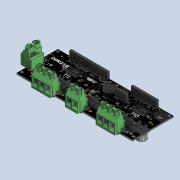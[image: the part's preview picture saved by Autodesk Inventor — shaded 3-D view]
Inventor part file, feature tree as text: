
AUTODESK INVENTOR PART (.ipt)
format: ipt  version: 2020 (Build 240168000, 168)  size: 21,689,856 bytes
history: native  units: mm
features: other x279, sketch x3
ambient origin geometry x8: Origin, YZ Plane, XZ Plane, XY Plane, X Axis, Y Axis, Z Axis, Center Point
bodies: Solid1 (feature_tree)
feature tree (282):
  other  "PCBasembly.iam"
  other  "Board.ipt:1"
  other  "R58.iam:1::RES_0603_(1608_metric).ipt:1"
  other  "LED1.iam:1::LED_0603_APT1608_GREEN.ipt:1"
  other  "TP3.iam:1::886587760.iam:1::Cylinder.ipt:1"
  other  "TP2.iam:1::886587760.iam:1::Cylinder.ipt:1"
  other  "TP1.iam:1::886587632.iam:1::Cylinder_1.ipt:1"
  other  "C48.iam:1::899959440.iam:1::Extruded.ipt:1"
  other  "C48.iam:1::899959304.iam:1::Extruded_1.ipt:1"
  other  "C48.iam:1::899959304.iam:2::Extruded_1.ipt:1"
  other  "R34.iam:1::RES_0603_(1608_metric).ipt:1"
  other  "R33.iam:1::RES_0603_(1608_metric).ipt:1"
  other  "R32.iam:1::RES_0603_(1608_metric).ipt:1"
  other  "R48.iam:1::RES_0603_(1608_metric).ipt:1"
  other  "R46.iam:1::899960256.iam:1::Extruded_3.ipt:1"
  other  "R46.iam:1::899960392.iam:1::Extruded_4.ipt:1"
  other  "R46.iam:1::899960256.iam:2::Extruded_3.ipt:1"
  other  "R45.iam:1::899960256.iam:1::Extruded_3.ipt:1"
  other  "R45.iam:1::899960392.iam:1::Extruded_4.ipt:1"
  other  "R45.iam:1::899960256.iam:2::Extruded_3.ipt:1"
  other  "R43.iam:1::RES_0603_(1608_metric).ipt:1"
  other  "R42.iam:1::RES_0603_(1608_metric).ipt:1"
  other  "R41.iam:1::RES_0603_(1608_metric).ipt:1"
  other  "R40.iam:1::RES_0603_(1608_metric).ipt:1"
  other  "R39.iam:1::RES_0603_(1608_metric).ipt:1"
  other  "R38.iam:1::RES_0603_(1608_metric).ipt:1"
  other  "R37.iam:1::RES_0603_(1608_metric).ipt:1"
  other  "R36.iam:1::RES_0603_(1608_metric).ipt:1"
  other  "R35.iam:1::RES_0603_(1608_metric).ipt:1"
  other  "C57.iam:1::899958488.iam:1::Extruded_5.ipt:1"
  other  "C57.iam:1::899958352.iam:1::Extruded_6.ipt:1"
  other  "C57.iam:1::899958352.iam:2::Extruded_6.ipt:1"
  other  "C56.iam:1::899958488.iam:1::Extruded_5.ipt:1"
  other  "C56.iam:1::899958352.iam:1::Extruded_6.ipt:1"
  other  "C56.iam:1::899958352.iam:2::Extruded_6.ipt:1"
  other  "C44.iam:1::899959032.iam:1::Extruded_7.ipt:1"
  other  "C44.iam:1::899959168.iam:1::Extruded_8.ipt:1"
  other  "C44.iam:1::899959032.iam:2::Extruded_7.ipt:1"
  other  "C52.iam:1::899959440.iam:1::Extruded.ipt:1"
  other  "C52.iam:1::899959304.iam:1::Extruded_1.ipt:1"
  other  "C52.iam:1::899959304.iam:2::Extruded_1.ipt:1"
  other  "C51.iam:1::899959440.iam:1::Extruded.ipt:1"
  other  "C51.iam:1::899959304.iam:1::Extruded_1.ipt:1"
  other  "C51.iam:1::899959304.iam:2::Extruded_1.ipt:1"
  other  "C50.iam:1::899959440.iam:1::Extruded.ipt:1"
  other  "C50.iam:1::899959304.iam:1::Extruded_1.ipt:1"
  other  "C50.iam:1::899959304.iam:2::Extruded_1.ipt:1"
  other  "C49.iam:1::899959440.iam:1::Extruded.ipt:1"
  other  "C49.iam:1::899959304.iam:1::Extruded_1.ipt:1"
  other  "C49.iam:1::899959304.iam:2::Extruded_1.ipt:1"
  other  "C47.iam:1::899959440.iam:1::Extruded.ipt:1"
  other  "C47.iam:1::899959304.iam:1::Extruded_1.ipt:1"
  other  "C47.iam:1::899959304.iam:2::Extruded_1.ipt:1"
  other  "C46.iam:1::899959440.iam:1::Extruded.ipt:1"
  other  "C46.iam:1::899959304.iam:1::Extruded_1.ipt:1"
  other  "C46.iam:1::899959304.iam:2::Extruded_1.ipt:1"
  other  "C45.iam:1::899959440.iam:1::Extruded.ipt:1"
  other  "C45.iam:1::899959304.iam:1::Extruded_1.ipt:1"
  other  "C45.iam:1::899959304.iam:2::Extruded_1.ipt:1"
  other  "C55.iam:1::899959032.iam:1::Extruded_7.ipt:1"
  other  "C55.iam:1::899959168.iam:1::Extruded_8.ipt:1"
  other  "C55.iam:1::899959032.iam:2::Extruded_7.ipt:1"
  other  "C18.iam:1::CAP_Alum_Elec_Size_G.ipt:1"
  other  "C17.iam:1::CAP_Alum_Elec_Size_G.ipt:1"
  other  "C16.iam:1::CAP_Alum_Elec_Size_G.ipt:1"
  other  "C43.iam:1::899958488.iam:1::Extruded_5.ipt:1"
  other  "C43.iam:1::899958352.iam:1::Extruded_6.ipt:1"
  other  "C43.iam:1::899958352.iam:2::Extruded_6.ipt:1"
  other  "C1.iam:1::899958488.iam:1::Extruded_5.ipt:1"
  other  "C1.iam:1::899958352.iam:1::Extruded_6.ipt:1"
  other  "C1.iam:1::899958352.iam:2::Extruded_6.ipt:1"
  other  "C2.iam:1::899958488.iam:1::Extruded_5.ipt:1"
  other  "C2.iam:1::899958352.iam:1::Extruded_6.ipt:1"
  other  "C2.iam:1::899958352.iam:2::Extruded_6.ipt:1"
  other  "C3.iam:1::899958488.iam:1::Extruded_5.ipt:1"
  other  "C3.iam:1::899958352.iam:1::Extruded_6.ipt:1"
  other  "C3.iam:1::899958352.iam:2::Extruded_6.ipt:1"
  other  "C4.iam:1::899958488.iam:1::Extruded_5.ipt:1"
  other  "C4.iam:1::899958352.iam:1::Extruded_6.ipt:1"
  other  "C4.iam:1::899958352.iam:2::Extruded_6.ipt:1"
  other  "C5.iam:1::899958488.iam:1::Extruded_5.ipt:1"
  other  "C5.iam:1::899958352.iam:1::Extruded_6.ipt:1"
  other  "C5.iam:1::899958352.iam:2::Extruded_6.ipt:1"
  other  "C6.iam:1::899958488.iam:1::Extruded_5.ipt:1"
  other  "C6.iam:1::899958352.iam:1::Extruded_6.ipt:1"
  other  "C6.iam:1::899958352.iam:2::Extruded_6.ipt:1"
  other  "C7.iam:1::899958488.iam:1::Extruded_5.ipt:1"
  other  "C7.iam:1::899958352.iam:1::Extruded_6.ipt:1"
  other  "C7.iam:1::899958352.iam:2::Extruded_6.ipt:1"
  other  "C8.iam:1::899958488.iam:1::Extruded_5.ipt:1"
  other  "C8.iam:1::899958352.iam:1::Extruded_6.ipt:1"
  other  "C8.iam:1::899958352.iam:2::Extruded_6.ipt:1"
  other  "C9.iam:1::899958488.iam:1::Extruded_5.ipt:1"
  other  "C9.iam:1::899958352.iam:1::Extruded_6.ipt:1"
  other  "C9.iam:1::899958352.iam:2::Extruded_6.ipt:1"
  other  "C10.iam:1::899958488.iam:1::Extruded_5.ipt:1"
  other  "C10.iam:1::899958352.iam:1::Extruded_6.ipt:1"
  other  "C10.iam:1::899958352.iam:2::Extruded_6.ipt:1"
  other  "C11.iam:1::CAP_Alum_Elec_Size_G.ipt:1"
  other  "C12.iam:1::CAP_Alum_Elec_Size_G.ipt:1"
  other  "C13.iam:1::CAP_Alum_Elec_Size_G.ipt:1"
  other  "C14.iam:1::CAP_Alum_Elec_Size_G.ipt:1"
  other  "C15.iam:1::CAP_Alum_Elec_Size_G.ipt:1"
  other  "C20.iam:1::899959032.iam:1::Extruded_7.ipt:1"
  other  "C20.iam:1::899959032.iam:2::Extruded_7.ipt:1"
  other  "C20.iam:1::899959168.iam:1::Extruded_8.ipt:1"
  other  "C21.iam:1::899959032.iam:1::Extruded_7.ipt:1"
  other  "C21.iam:1::899959032.iam:2::Extruded_7.ipt:1"
  other  "C21.iam:1::899959168.iam:1::Extruded_8.ipt:1"
  other  "C22.iam:1::899959440.iam:1::Extruded.ipt:1"
  other  "C22.iam:1::899959304.iam:1::Extruded_1.ipt:1"
  other  "C22.iam:1::899959304.iam:2::Extruded_1.ipt:1"
  other  "C23.iam:1::899958488.iam:1::Extruded_5.ipt:1"
  other  "C23.iam:1::899958352.iam:1::Extruded_6.ipt:1"
  other  "C23.iam:1::899958352.iam:2::Extruded_6.ipt:1"
  other  "C24.iam:1::899959440.iam:1::Extruded.ipt:1"
  other  "C24.iam:1::899959304.iam:1::Extruded_1.ipt:1"
  other  "C24.iam:1::899959304.iam:2::Extruded_1.ipt:1"
  other  "C25.iam:1::899959440.iam:1::Extruded.ipt:1"
  other  "C25.iam:1::899959304.iam:1::Extruded_1.ipt:1"
  other  "C25.iam:1::899959304.iam:2::Extruded_1.ipt:1"
  other  "C26.iam:1::899959032.iam:1::Extruded_7.ipt:1"
  other  "C26.iam:1::899959168.iam:1::Extruded_8.ipt:1"
  other  "C26.iam:1::899959032.iam:2::Extruded_7.ipt:1"
  other  "C27.iam:1::899959440.iam:1::Extruded.ipt:1"
  other  "C27.iam:1::899959304.iam:1::Extruded_1.ipt:1"
  other  "C27.iam:1::899959304.iam:2::Extruded_1.ipt:1"
  other  "C28.iam:1::899959440.iam:1::Extruded.ipt:1"
  other  "C28.iam:1::899959304.iam:1::Extruded_1.ipt:1"
  other  "C28.iam:1::899959304.iam:2::Extruded_1.ipt:1"
  other  "C29.iam:1::899958760.iam:1::Extruded_9.ipt:1"
  other  "C29.iam:1::899958896.iam:1::Extruded_10.ipt:1"
  other  "C29.iam:1::899958760.iam:2::Extruded_9.ipt:1"
  other  "C30.iam:1::899959440.iam:1::Extruded.ipt:1"
  other  "C30.iam:1::899959304.iam:1::Extruded_1.ipt:1"
  other  "C30.iam:1::899959304.iam:2::Extruded_1.ipt:1"
  other  "C31.iam:1::899959440.iam:1::Extruded.ipt:1"
  other  "C31.iam:1::899959304.iam:1::Extruded_1.ipt:1"
  other  "C31.iam:1::899959304.iam:2::Extruded_1.ipt:1"
  other  "C32.iam:1::899958488.iam:1::Extruded_5.ipt:1"
  other  "C32.iam:1::899958352.iam:1::Extruded_6.ipt:1"
  other  "C32.iam:1::899958352.iam:2::Extruded_6.ipt:1"
  other  "C33.iam:1::899959440.iam:1::Extruded.ipt:1"
  other  "C33.iam:1::899959304.iam:1::Extruded_1.ipt:1"
  other  "C33.iam:1::899959304.iam:2::Extruded_1.ipt:1"
  other  "C34.iam:1::899959440.iam:1::Extruded.ipt:1"
  other  "C34.iam:1::899959304.iam:1::Extruded_1.ipt:1"
  other  "C34.iam:1::899959304.iam:2::Extruded_1.ipt:1"
  other  "C35.iam:1::899959440.iam:1::Extruded.ipt:1"
  other  "C35.iam:1::899959304.iam:1::Extruded_1.ipt:1"
  other  "C35.iam:1::899959304.iam:2::Extruded_1.ipt:1"
  other  "C36.iam:1::899959440.iam:1::Extruded.ipt:1"
  other  "C36.iam:1::899959304.iam:1::Extruded_1.ipt:1"
  other  "C36.iam:1::899959304.iam:2::Extruded_1.ipt:1"
  other  "C37.iam:1::899958488.iam:1::Extruded_5.ipt:1"
  other  "C37.iam:1::899958352.iam:1::Extruded_6.ipt:1"
  other  "C37.iam:1::899958352.iam:2::Extruded_6.ipt:1"
  other  "C40.iam:1::899959032.iam:1::Extruded_7.ipt:1"
  other  "C40.iam:1::899959168.iam:1::Extruded_8.ipt:1"
  other  "C40.iam:1::899959032.iam:2::Extruded_7.ipt:1"
  other  "C41.iam:1::899958488.iam:1::Extruded_5.ipt:1"
  other  "C41.iam:1::899958352.iam:1::Extruded_6.ipt:1"
  other  "C41.iam:1::899958352.iam:2::Extruded_6.ipt:1"
  other  "C42.iam:1::899958488.iam:1::Extruded_5.ipt:1"
  other  "C42.iam:1::899958352.iam:1::Extruded_6.ipt:1"
  other  "C42.iam:1::899958352.iam:2::Extruded_6.ipt:1"
  other  "C58.iam:1::899958488.iam:1::Extruded_5.ipt:1"
  other  "C58.iam:1::899958352.iam:1::Extruded_6.ipt:1"
  other  "C58.iam:1::899958352.iam:2::Extruded_6.ipt:1"
  other  "C59.iam:1::899959440.iam:1::Extruded.ipt:1"
  other  "C59.iam:1::899959304.iam:1::Extruded_1.ipt:1"
  other  "C59.iam:1::899959304.iam:2::Extruded_1.ipt:1"
  other  "C61.iam:1::899958488.iam:1::Extruded_5.ipt:1"
  other  "C61.iam:1::899958352.iam:1::Extruded_6.ipt:1"
  other  "C61.iam:1::899958352.iam:2::Extruded_6.ipt:1"
  other  "C62.iam:1::899959440.iam:1::Extruded.ipt:1"
  other  "C62.iam:1::899959304.iam:1::Extruded_1.ipt:1"
  other  "C62.iam:1::899959304.iam:2::Extruded_1.ipt:1"
  other  "C63.iam:1::899959440.iam:1::Extruded.ipt:1"
  other  "C63.iam:1::899959304.iam:1::Extruded_1.ipt:1"
  other  "C63.iam:1::899959304.iam:2::Extruded_1.ipt:1"
  other  "D1.iam:1::899958624.iam:1::Extruded_11.ipt:1"
  other  "D2.iam:1::899958624.iam:1::Extruded_11.ipt:1"
  other  "L2.iam:1::899960800.iam:1::Extruded_12.ipt:1"
  other  "L2.iam:1::899960936.iam:1::Extruded_13.ipt:1"
  other  "L2.iam:1::899960936.iam:2::Extruded_13.ipt:1"
  other  "R1.iam:1::RES_0603_(1608_metric).ipt:1"
  other  "R3.iam:1::RES_0603_(1608_metric).ipt:1"
  other  "R5.iam:1::RES_0603_(1608_metric).ipt:1"
  other  "R6.iam:1::RES_0603_(1608_metric).ipt:1"
  other  "R7.iam:1::RES_0603_(1608_metric).ipt:1"
  other  "R8.iam:1::RES_0603_(1608_metric).ipt:1"
  other  "R9.iam:1::RES_0603_(1608_metric).ipt:1"
  other  "R10.iam:1::RES_0603_(1608_metric).ipt:1"
  other  "R11.iam:1::RES_0603_(1608_metric).ipt:1"
  other  "R13.iam:1::RES_0603_(1608_metric).ipt:1"
  other  "R14.iam:1::RES_0603_(1608_metric).ipt:1"
  other  "R15.iam:1::RES_0603_(1608_metric).ipt:1"
  other  "R16.iam:1::RES_0603_(1608_metric).ipt:1"
  other  "R17.iam:1::RES_0603_(1608_metric).ipt:1"
  other  "R18.iam:1::RES_0603_(1608_metric).ipt:1"
  other  "R19.iam:1::RES_0603_(1608_metric).ipt:1"
  other  "R20.iam:1::RES_0603_(1608_metric).ipt:1"
  other  "R21.iam:1::RES_0603_(1608_metric).ipt:1"
  other  "R22.iam:1::RES_0603_(1608_metric).ipt:1"
  other  "R23.iam:1::RES_0603_(1608_metric).ipt:1"
  other  "R24.iam:1::RES_0603_(1608_metric).ipt:1"
  other  "R25.iam:1::RES_0603_(1608_metric).ipt:1"
  other  "R27.iam:1::899960256.iam:1::Extruded_3.ipt:1"
  other  "R27.iam:1::899960392.iam:1::Extruded_4.ipt:1"
  other  "R27.iam:1::899960256.iam:2::Extruded_3.ipt:1"
  other  "R28.iam:1::899960256.iam:1::Extruded_3.ipt:1"
  other  "R28.iam:1::899960392.iam:1::Extruded_4.ipt:1"
  other  "R28.iam:1::899960256.iam:2::Extruded_3.ipt:1"
  other  "R30.iam:1::RES_0603_(1608_metric).ipt:1"
  other  "R50.iam:1::RES_0603_(1608_metric).ipt:1"
  other  "R51.iam:1::RES_0603_(1608_metric).ipt:1"
  other  "R54.iam:1::RES_0603_(1608_metric).ipt:1"
  other  "R56.iam:1::899960256.iam:1::Extruded_3.ipt:1"
  other  "R56.iam:1::899960392.iam:1::Extruded_4.ipt:1"
  other  "R56.iam:1::899960256.iam:2::Extruded_3.ipt:1"
  other  "R55.iam:1::RES_0603_(1608_metric).ipt:1"
  other  "U3.iam:1::SOT223-4.ipt:1"
  other  "U6.iam:1::899959984.iam:1::Extruded_14.ipt:1"
  other  "U7.iam:1::899960664.iam:1::Extruded_15.ipt:1"
  other  "XT1.iam:1::899960528.iam:1::Extruded_16.ipt:1"
  other  "U1.iam:1::899960664.iam:1::Extruded_15.ipt:1"
  other  "R2.iam:1::RES_0603_(1608_metric).ipt:1"
  other  "R4.iam:1::RES_0603_(1608_metric).ipt:1"
  other  "C38.iam:1::899959440.iam:1::Extruded.ipt:1"
  other  "C38.iam:1::899959304.iam:1::Extruded_1.ipt:1"
  other  "C38.iam:1::899959304.iam:2::Extruded_1.ipt:1"
  other  "C39.iam:1::899959440.iam:1::Extruded.ipt:1"
  other  "C39.iam:1::899959304.iam:1::Extruded_1.ipt:1"
  other  "C39.iam:1::899959304.iam:2::Extruded_1.ipt:1"
  other  "C53.iam:1::899958488.iam:1::Extruded_5.ipt:1"
  other  "C53.iam:1::899958352.iam:1::Extruded_6.ipt:1"
  other  "C53.iam:1::899958352.iam:2::Extruded_6.ipt:1"
  other  "C54.iam:1::899958488.iam:1::Extruded_5.ipt:1"
  other  "C54.iam:1::899958352.iam:1::Extruded_6.ipt:1"
  other  "C54.iam:1::899958352.iam:2::Extruded_6.ipt:1"
  other  "R26.iam:1::RES_0603_(1608_metric).ipt:1"
  other  "R29.iam:1::RES_0603_(1608_metric).ipt:1"
  other  "R44.iam:1::RES_0603_(1608_metric).ipt:1"
  other  "R47.iam:1::RES_0603_(1608_metric).ipt:1"
  other  "R12.iam:1::RES_0402_(1005_metric).ipt:1"
  other  "R31.iam:1::RES_0402_(1005_metric).ipt:1"
  other  "R49.iam:1::RES_0402_(1005_metric).ipt:1"
  other  "C64.iam:1::899958352.iam:1::Extruded_6.ipt:1"
  other  "C64.iam:1::899958352.iam:2::Extruded_6.ipt:1"
  other  "C64.iam:1::899958488.iam:1::Extruded_5.ipt:1"
  other  "R57.iam:1::899959712.iam:1::Extruded_18.ipt:1"
  other  "R57.iam:1::899959712.iam:2::Extruded_18.ipt:1"
  other  "R57.iam:1::899959848.iam:1::Extruded_19.ipt:1"
  other  "C65.iam:1::899959304.iam:1::Extruded_1.ipt:1"
  other  "C65.iam:1::899959304.iam:2::Extruded_1.ipt:1"
  other  "C65.iam:1::899959440.iam:1::Extruded.ipt:1"
  other  "U8.iam:1::SOT23-5.ipt:1"
  other  "C19.iam:1::899959032.iam:1::Extruded_7.ipt:1"
  other  "C19.iam:1::899959168.iam:1::Extruded_8.ipt:1"
  other  "C19.iam:1::899959032.iam:2::Extruded_7.ipt:1"
  other  "C60.iam:1::899958080.iam:1::Extruded_20.ipt:1"
  other  "C60.iam:1::899958216.iam:1::Extruded_21.ipt:1"
  other  "C60.iam:1::899958216.iam:2::Extruded_21.ipt:1"
  other  "partmicro_usb_connector_Shrinkwrap_1.ipt:1"
  other  "mkds_5-3-7.62.ipt:1"
  other  "mkds_5-3-7.62.ipt:2"
  other  "mkds_5-2-7.62.ipt:1"
  other  "mkds_5-2-7.62.ipt:2"
  other  "2DCA56_6P35X3P61.ipt:1"
  other  "2DCA56_6P35X3P61.ipt:2"
  other  "2LQFP-64.ipt:1"
  other  "5pin.ipt:1"
  other  "_18_pin.ipt:1"
  other  "_12_pin.ipt:1"
  other  "Decal1"
  other  "Decal2"
  sketch  "Sketch 1"  dims[d0=10.0mm]
  sketch  "Sketch2"
  other  "Image1"
  sketch  "Sketch3"
  other  "Image2"
